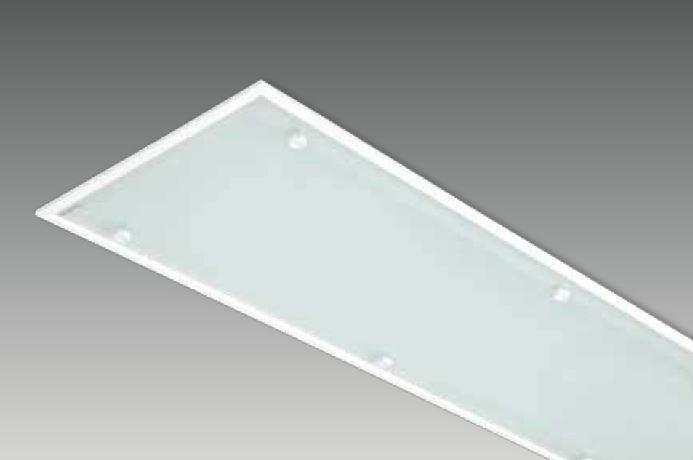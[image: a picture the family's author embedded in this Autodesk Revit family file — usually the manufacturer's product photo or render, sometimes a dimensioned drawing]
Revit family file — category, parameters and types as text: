
# Revit family: E 3012 GAC
name_source: partatom
category: Lighting Fixtures
revit_build: Autodesk Revit 2017 (Build: 20160225_1515(x64)
units: mm (PartAtom-declared; Revit-internal decimal feet)

## family parameters
Always vertical = Yes
Cut with Voids When Loaded = No
Host = Ceiling
Light Source = Yes
OmniClass Number = 23.80.70.11
OmniClass Title = Luminaries for Internal Lighting
Part Type = Normal
Room Calculation Point = No
Round Connector Dimension = Use Diameter
Shared = No

## types (2) — shared parameters
Apparent Load = 32 VA
Color Filter = 16777215
Dimming Lamp Color Temperature Shift = <None>
Emit Shape Visible in Rendering = Yes
Emit from Rectangle Length = 210 mm  [stored 0.688976 ft]
Emit from Rectangle Width = 1140 mm  [stored 3.74016 ft]
Light Source Symbol Size = 610 mm
Manufacturer = ARLIGHT
Type Image = E 3012 GAC.JPG
Wattage Comments = 32

## type names (no varying parameters)
- EGAC.3012.32.30
- EGAC.3012.32.40

note: [stored X ft] marks values corroborated as IEEE doubles in the binary element streams (Revit-internal decimal feet)

## geometry (parser evidence)
native form markers: Sweep x2
no freeform markers — native parametric forms only
